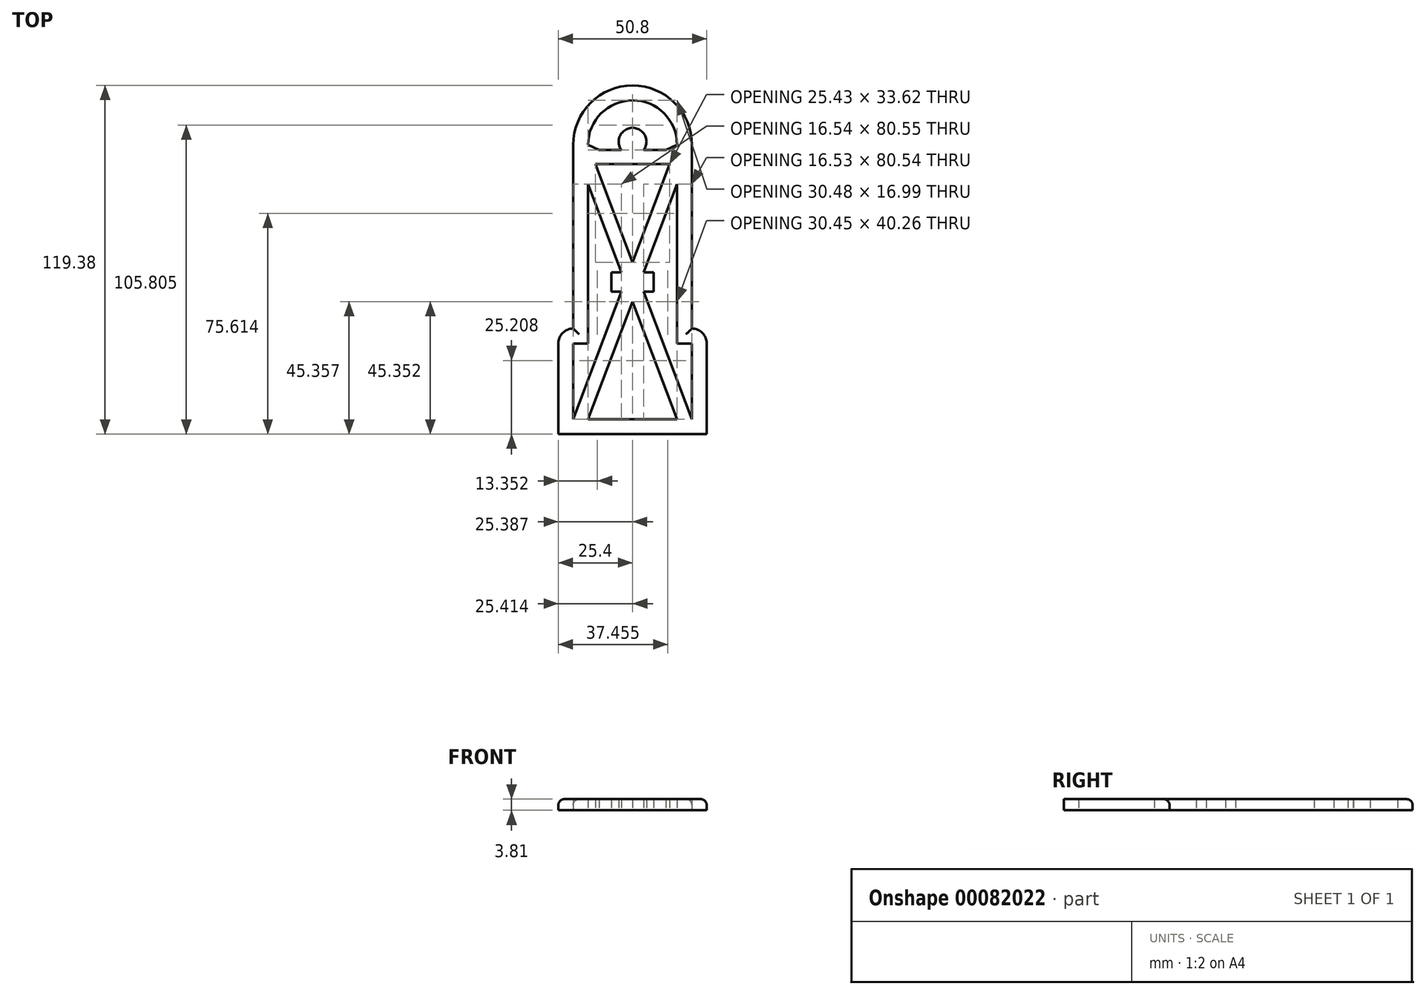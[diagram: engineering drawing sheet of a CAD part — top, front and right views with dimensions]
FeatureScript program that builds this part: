
annotation { "Feature Type Name" : "Feature", "Feature Type Description" : "" }
export const myFeature = defineFeature(function(context is Context, id is Id, definition is map)
    precondition{}
    {
        {
            var Q0;
            Q0=qCreatedBy(makeId("Top.planeOp"),FACE);
            var sketch = newSketch(context, id + "F0", { "sketchPlane" : qUnion([Q0])});
            skLineSegment(sketch, "E0", {"start": v(0, 0) * mm, "end": v(50.8, 0) * mm});
            skLineSegment(sketch, "E1", {"start": v(50.8, 0) * mm, "end": v(50.8, 36.16) * mm});
            skLineSegment(sketch, "E2", {"start": v(50.8, 36.16) * mm, "end": v(45.72, 36.16) * mm});
            skLineSegment(sketch, "E3", {"start": v(45.72, 36.16) * mm, "end": v(45.72, 99.06) * mm});
            skLineSegment(sketch, "E4", {"start": v(0, 0) * mm, "end": v(0, 36.16) * mm});
            skLineSegment(sketch, "E5", {"start": v(0, 36.16) * mm, "end": v(5.08, 36.16) * mm});
            skLineSegment(sketch, "E6", {"start": v(5.08, 36.16) * mm, "end": v(5.08, 99.06) * mm});
            skArc(sketch, "E7", {"start": v(45.72, 99.06) * mm, "mid": v(25.4, 119.38) * mm, "end": v(5.08, 99.06) * mm});
            skLineSegment(sketch, "E8", {"start": v(10.19, 5.08) * mm, "end": v(40.64, 5.08) * mm});
            skLineSegment(sketch, "E9", {"start": v(45.72, 5.08) * mm, "end": v(45.72, 30.95) * mm});
            skLineSegment(sketch, "E10", {"start": v(45.72, 30.95) * mm, "end": v(40.64, 30.95) * mm});
            skLineSegment(sketch, "E11", {"start": v(40.64, 30.95) * mm, "end": v(40.64, 85.62) * mm});
            skLineSegment(sketch, "E12", {"start": v(5.08, 5.08) * mm, "end": v(5.08, 30.95) * mm});
            skLineSegment(sketch, "E13", {"start": v(5.08, 30.95) * mm, "end": v(10.16, 30.95) * mm});
            skLineSegment(sketch, "E14", {"start": v(10.16, 30.95) * mm, "end": v(10.16, 85.63) * mm});
            skArc(sketch, "E15", {"start": v(40.64, 99.13) * mm, "mid": v(25.36, 114.3) * mm, "end": v(10.16, 99.06) * mm});
            skPoint(sketch, "E16.middle", {"position": v(25.4, 58.8) * mm});
            skLineSegment(sketch, "E17.trimOffspring", {"start": v(21.6, 48.77) * mm, "end": v(5.08, 5.08) * mm});
            skLineSegment(sketch, "E18.trimOffspring", {"start": v(29.2, 48.77) * mm, "end": v(45.72, 5.08) * mm});
            skLineSegment(sketch, "E19.trimOffspring", {"start": v(25.4, 45.34) * mm, "end": v(40.64, 5.08) * mm});
            skLineSegment(sketch, "E20.trimOffspring", {"start": v(25.4, 45.34) * mm, "end": v(10.19, 5.08) * mm});
            skLineSegment(sketch, "E21", {"start": v(10.16, 99.06) * mm, "end": v(13.9, 97.3) * mm});
            skLineSegment(sketch, "E22", {"start": v(12.67, 92.42) * mm, "end": v(24.33, 92.42) * mm});
            skLineSegment(sketch, "E23", {"start": v(38.1, 92.42) * mm, "end": v(26.47, 92.42) * mm});
            skLineSegment(sketch, "E24", {"start": v(40.64, 99.13) * mm, "end": v(36.79, 97.3) * mm});
            skLineSegment(sketch, "E25", {"start": v(21.58, 97.3) * mm, "end": v(13.9, 97.3) * mm});
            skLineSegment(sketch, "E26", {"start": v(29.22, 97.3) * mm, "end": v(36.79, 97.3) * mm});
            skArc(sketch, "E27", {"start": v(29.22, 97.3) * mm, "mid": v(25.4, 104.87) * mm, "end": v(21.58, 97.3) * mm});
            skLineSegment(sketch, "E28", {"start": v(40.64, 85.62) * mm, "end": v(29.19, 55.34) * mm});
            skLineSegment(sketch, "E29", {"start": v(10.16, 85.63) * mm, "end": v(21.62, 55.34) * mm});
            skLineSegment(sketch, "E30", {"start": v(24.33, 92.42) * mm, "end": v(26.47, 92.42) * mm});
            skLineSegment(sketch, "E31", {"start": v(38.1, 92.42) * mm, "end": v(25.4, 58.8) * mm});
            skLineSegment(sketch, "E32", {"start": v(12.67, 92.42) * mm, "end": v(25.4, 58.8) * mm});
            skLineSegment(sketch, "E33.bottom", {"start": v(32.6, 48.77) * mm, "end": v(29.2, 48.77) * mm});
            skLineSegment(sketch, "E33.top", {"start": v(32.6, 55.34) * mm, "end": v(29.19, 55.34) * mm});
            skLineSegment(sketch, "E33.left", {"start": v(32.6, 48.77) * mm, "end": v(32.6, 55.34) * mm});
            skLineSegment(sketch, "E33.right", {"start": v(18.19, 48.77) * mm, "end": v(18.19, 55.34) * mm});
            skPoint(sketch, "E33.middle", {"position": v(25.4, 52.05) * mm});
            skLineSegment(sketch, "E34.trimOffspring", {"start": v(21.62, 55.34) * mm, "end": v(18.19, 55.34) * mm});
            skLineSegment(sketch, "E35.trimOffspring", {"start": v(21.6, 48.77) * mm, "end": v(18.19, 48.77) * mm});
            skSolve(sketch);
        }
        {
            var Q0;
            Q0 = qSketchRegion(id + "F0", true);
            extrude(context, id + "F1", {"entities" : qUnion([Q0]), "depth" : 3.8 * mm});
        }
        {
            var Q0;
            Q0=makeQuery(id+"F1.opExtrude","CAP_EDGE",EDGE,{"disambiguationData":[OSD([sQuery(id+"F0.wireOp",EDGE,"E3")])],"isStart":false});
            var Q1;
            Q1=makeQuery(id+"F1.opExtrude","CAP_EDGE",EDGE,{"disambiguationData":[OSD([sQuery(id+"F0.wireOp",EDGE,"E1")])],"isStart":false});
            var Q2;
            Q2=makeQuery(id+"F1.opExtrude","CAP_EDGE",EDGE,{"disambiguationData":[OSD([sQuery(id+"F0.wireOp",EDGE,"E2")])],"isStart":false});
            var Q3;
            Q3=makeQuery(id+"F1.opExtrude","CAP_EDGE",EDGE,{"disambiguationData":[OSD([sQuery(id+"F0.wireOp",EDGE,"E5")])],"isStart":false});
            var Q4;
            Q4=makeQuery(id+"F1.opExtrude","CAP_EDGE",EDGE,{"disambiguationData":[OSD([sQuery(id+"F0.wireOp",EDGE,"E4")])],"isStart":false});
            fillet(context, id + "F2", {"entities" : qUnion([Q0, Q1, Q2, Q3, Q4]), "radius" : 2.03 * mm, "tangentPropagation" : true, "allowEdgeOverflow" : false});
        }
        {
            var Q0;
            Q0=makeQuery(id+"F1.opExtrude","SWEPT_EDGE",EDGE,{"disambiguationData":[OSD([sQuery(id+"F0.wireOp",EDGE,"E1"),sQuery(id+"F0.wireOp",EDGE,"E2")])]});
            var Q1;
            Q1=makeQuery(id+"F1.opExtrude","SWEPT_EDGE",EDGE,{"disambiguationData":[OSD([sQuery(id+"F0.wireOp",EDGE,"E4"),sQuery(id+"F0.wireOp",EDGE,"E5")])]});
            fillet(context, id + "F3", {"entities" : qUnion([Q0, Q1]), "radius" : 5.08 * mm, "tangentPropagation" : true, "allowEdgeOverflow" : false});
        }
    });
